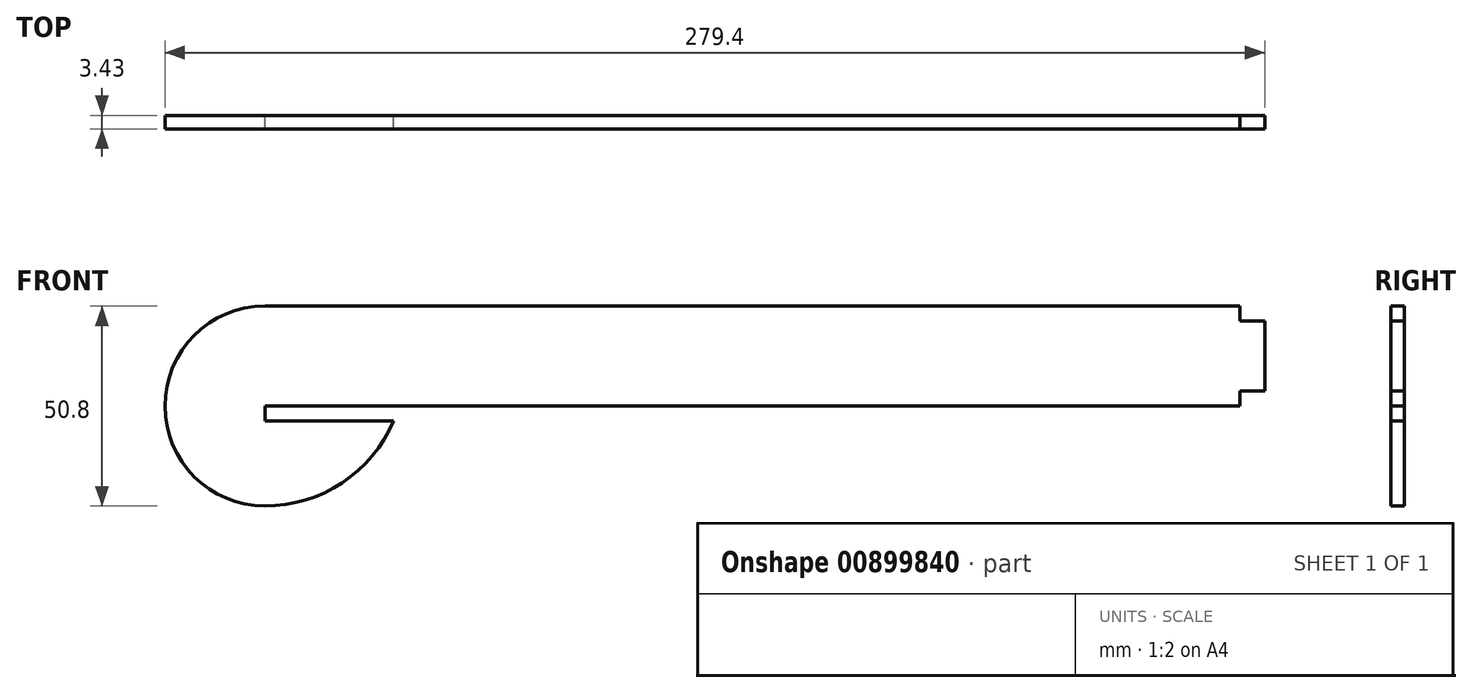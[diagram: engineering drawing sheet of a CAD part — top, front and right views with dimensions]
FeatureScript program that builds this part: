
annotation { "Feature Type Name" : "Feature", "Feature Type Description" : "" }
export const myFeature = defineFeature(function(context is Context, id is Id, definition is map)
    precondition{}
    {
        {
            var Q0;
            Q0=qCreatedBy(makeId("Front.planeOp"),FACE);
            var sketch = newSketch(context, id + "F0", { "sketchPlane" : qUnion([Q0])});
            skLineSegment(sketch, "E0", {"start": v(412.52, 414.56) * mm, "end": v(164.87, 414.56) * mm});
            skLineSegment(sketch, "E1", {"start": v(412.52, 410.75) * mm, "end": v(412.52, 414.56) * mm});
            skLineSegment(sketch, "E2", {"start": v(418.87, 410.75) * mm, "end": v(412.52, 410.75) * mm});
            skLineSegment(sketch, "E3", {"start": v(418.87, 392.97) * mm, "end": v(418.87, 410.75) * mm});
            skLineSegment(sketch, "E4", {"start": v(412.52, 392.97) * mm, "end": v(418.87, 392.97) * mm});
            skLineSegment(sketch, "E5", {"start": v(164.87, 385.35) * mm, "end": v(164.87, 389.16) * mm});
            skLineSegment(sketch, "E6", {"start": v(197.63, 385.35) * mm, "end": v(164.87, 385.35) * mm});
            skArc(sketch, "E7", {"start": v(164.87, 363.76) * mm, "mid": v(184.49, 369.65) * mm, "end": v(197.63, 385.35) * mm});
            skLineSegment(sketch, "E8", {"start": v(412.52, 389.16) * mm, "end": v(412.52, 392.97) * mm});
            skLineSegment(sketch, "E9", {"start": v(164.87, 389.16) * mm, "end": v(412.52, 389.16) * mm});
            skArc(sketch, "E10", {"start": v(164.87, 414.56) * mm, "mid": v(139.47, 389.16) * mm, "end": v(164.87, 363.76) * mm});
            skSolve(sketch);
        }
        {
            var Q0;
            Q0 = qSketchRegion(id + "F0", true);
            extrude(context, id + "F1", {"entities" : qUnion([Q0]), "depth" : 3.43 * mm, "offsetDistance" : 25.4 * mm});
        }
    });
